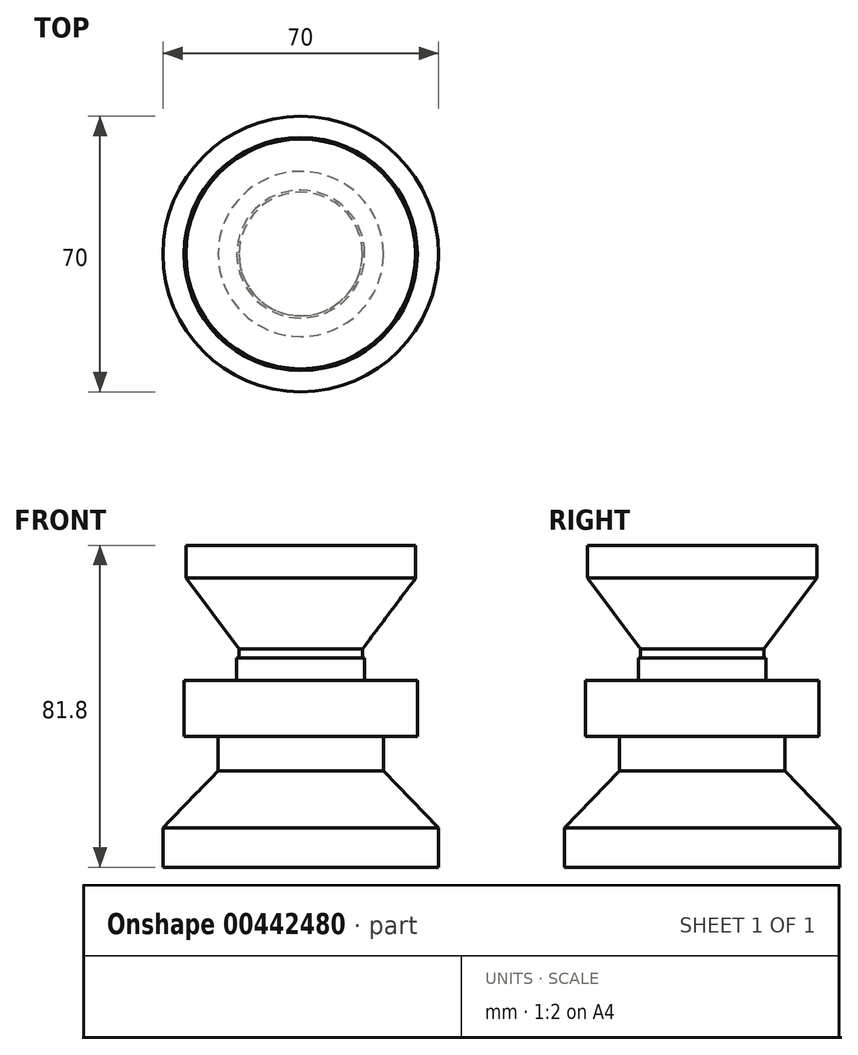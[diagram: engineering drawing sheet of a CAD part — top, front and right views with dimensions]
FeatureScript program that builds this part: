
annotation { "Feature Type Name" : "Feature", "Feature Type Description" : "" }
export const myFeature = defineFeature(function(context is Context, id is Id, definition is map)
    precondition{}
    {
        {
            var Q0;
            Q0=qCreatedBy(makeId("Top.planeOp"),FACE);
            var sketch = newSketch(context, id + "F0", { "sketchPlane" : qUnion([Q0])});
            skCircle(sketch, "E0", {"center": v(0, 0) * mm, "radius": 29.18 * mm});
            skSolve(sketch);
        }
        {
            var Q0;
            Q0=qSketchRegion(id+"F0",true);
            extrude(context, id + "F1", {"entities" : qUnion([Q0]), "depth" : 8.35 * mm});
        }
        {
            var Q0;
            Q0=makeQuery(id+"F1.opExtrude","CAP_FACE",FACE,{"disambiguationData":[OSD([sQuery(id+"F0.wireOp",EDGE,"E0")])],"isStart":true});
            cPlane(context, id + "F2", {"entities" : qUnion([Q0]), "cplaneType" : CPlaneType.OFFSET, "offset" : 18 * mm, "width" : 150 * mm, "height" : 150 * mm});
        }
        {
            var Q0;
            Q0=qCreatedBy(id+"F2.planeOp",FACE);
            var sketch = newSketch(context, id + "F3", { "sketchPlane" : qUnion([Q0])});
            skCircle(sketch, "E1", {"center": v(0, 0) * mm, "radius": 15.69 * mm});
            skSolve(sketch);
        }
        {
            var Q1;
            Q1=makeQuery(id+"F1.opExtrude","CAP_FACE",FACE,{"disambiguationData":[OSD([sQuery(id+"F0.wireOp",EDGE,"E0")])],"isStart":true});
            var Q2;
            Q2=makeQuery(id+"F3.imprint","IMPRINT",FACE,{"disambiguationData":[TD([[makeQuery(id+"F3.imprint","IMPRINT",EDGE,{"derivedFrom":sQuery(id+"F3.wireOp",EDGE,"E1")}),1.0]])]});
            loft(context, id + "F4", {"operationType" : NewBodyOperationType.ADD, "sheetProfilesArray" : [{ "sheetProfileEntities" : qUnion([Q1]) }, { "sheetProfileEntities" : qUnion([Q2]) }]});
        }
        {
            var Q0;
            Q0=makeQuery(id+"F4.opLoft","CAP_FACE",FACE,{"disambiguationData":[OSD([makeQuery(id+"F3.imprint","IMPRINT",FACE,{"disambiguationData":[TD([[makeQuery(id+"F3.imprint","IMPRINT",EDGE,{"derivedFrom":sQuery(id+"F3.wireOp",EDGE,"E1")}),1.0]])]})])],"isStart":true});
            var sketch = newSketch(context, id + "F5", { "sketchPlane" : qUnion([Q0])});
            skCircle(sketch, "E2", {"center": v(0, 0) * mm, "radius": 15.69 * mm});
            skSolve(sketch);
        }
        {
            var Q0;
            Q0=qSketchRegion(id+"F5",true);
            extrude(context, id + "F6", {"entities" : qUnion([Q0]), "operationType" : NewBodyOperationType.ADD, "depth" : 2.25 * mm});
        }
        {
            var Q0;
            Q0=makeQuery(id+"F6.opExtrude","CAP_FACE",FACE,{"disambiguationData":[OSD([sQuery(id+"F5.wireOp",EDGE,"E2")])],"isStart":false});
            var sketch = newSketch(context, id + "F7", { "sketchPlane" : qUnion([Q0])});
            skCircle(sketch, "E3", {"center": v(0, 0) * mm, "radius": 16.25 * mm});
            skSolve(sketch);
        }
        {
            var Q0;
            Q0=qSketchRegion(id+"F7",true);
            extrude(context, id + "F8", {"entities" : qUnion([Q0]), "operationType" : NewBodyOperationType.ADD, "depth" : 5.75 * mm});
        }
        {
            var Q0;
            Q0=makeQuery(id+"F8.opExtrude","CAP_FACE",FACE,{"disambiguationData":[OSD([sQuery(id+"F7.wireOp",EDGE,"E3")])],"isStart":false});
            var sketch = newSketch(context, id + "F9", { "sketchPlane" : qUnion([Q0])});
            skCircle(sketch, "E4", {"center": v(0, 0) * mm, "radius": 29.63 * mm});
            skSolve(sketch);
        }
        {
            var Q0;
            Q0=qSketchRegion(id+"F9",true);
            extrude(context, id + "F10", {"entities" : qUnion([Q0]), "operationType" : NewBodyOperationType.ADD, "depth" : 14.2 * mm});
        }
        {
            var Q0;
            Q0=makeQuery(id+"F10.opExtrude","CAP_FACE",FACE,{"disambiguationData":[OSD([sQuery(id+"F9.wireOp",EDGE,"E4")])],"isStart":false});
            var sketch = newSketch(context, id + "F11", { "sketchPlane" : qUnion([Q0])});
            skCircle(sketch, "E5", {"center": v(0, 0) * mm, "radius": 21 * mm});
            skSolve(sketch);
        }
        {
            var Q0;
            Q0=qSketchRegion(id+"F11",true);
            extrude(context, id + "F12", {"entities" : qUnion([Q0]), "operationType" : NewBodyOperationType.ADD, "depth" : 8.75 * mm});
        }
        {
            var Q0;
            Q0=makeQuery(id+"F12.opExtrude","CAP_FACE",FACE,{"disambiguationData":[OSD([sQuery(id+"F11.wireOp",EDGE,"E5")])],"isStart":false});
            cPlane(context, id + "F13", {"entities" : qUnion([Q0]), "cplaneType" : CPlaneType.OFFSET, "offset" : 14.5 * mm, "width" : 150 * mm, "height" : 150 * mm});
        }
        {
            var Q0;
            Q0=qCreatedBy(id+"F13.planeOp",FACE);
            var sketch = newSketch(context, id + "F14", { "sketchPlane" : qUnion([Q0])});
            skCircle(sketch, "E6", {"center": v(0, 0) * mm, "radius": 35 * mm});
            skSolve(sketch);
        }
        {
            var Q1;
            Q1=makeQuery(id+"F12.opExtrude","CAP_FACE",FACE,{"disambiguationData":[OSD([sQuery(id+"F11.wireOp",EDGE,"E5")])],"isStart":false});
            var Q2;
            Q2=makeQuery(id+"F14.imprint","IMPRINT",FACE,{"disambiguationData":[TD([[makeQuery(id+"F14.imprint","IMPRINT",EDGE,{"derivedFrom":sQuery(id+"F14.wireOp",EDGE,"E6")}),1.0]])]});
            loft(context, id + "F15", {"operationType" : NewBodyOperationType.ADD, "sheetProfilesArray" : [{ "sheetProfileEntities" : qUnion([Q1]) }, { "sheetProfileEntities" : qUnion([Q2]) }]});
        }
        {
            var Q0;
            Q0=makeQuery(id+"F15.opLoft","CAP_FACE",FACE,{"disambiguationData":[OSD([makeQuery(id+"F14.imprint","IMPRINT",FACE,{"disambiguationData":[TD([[makeQuery(id+"F14.imprint","IMPRINT",EDGE,{"derivedFrom":sQuery(id+"F14.wireOp",EDGE,"E6")}),1.0]])]})])],"isStart":true});
            var sketch = newSketch(context, id + "F16", { "sketchPlane" : qUnion([Q0])});
            skCircle(sketch, "E7", {"center": v(0, 0) * mm, "radius": 35 * mm});
            skSolve(sketch);
        }
        {
            var Q0;
            Q0=qSketchRegion(id+"F16",true);
            extrude(context, id + "F17", {"entities" : qUnion([Q0]), "operationType" : NewBodyOperationType.ADD, "depth" : 10 * mm});
        }
    });
